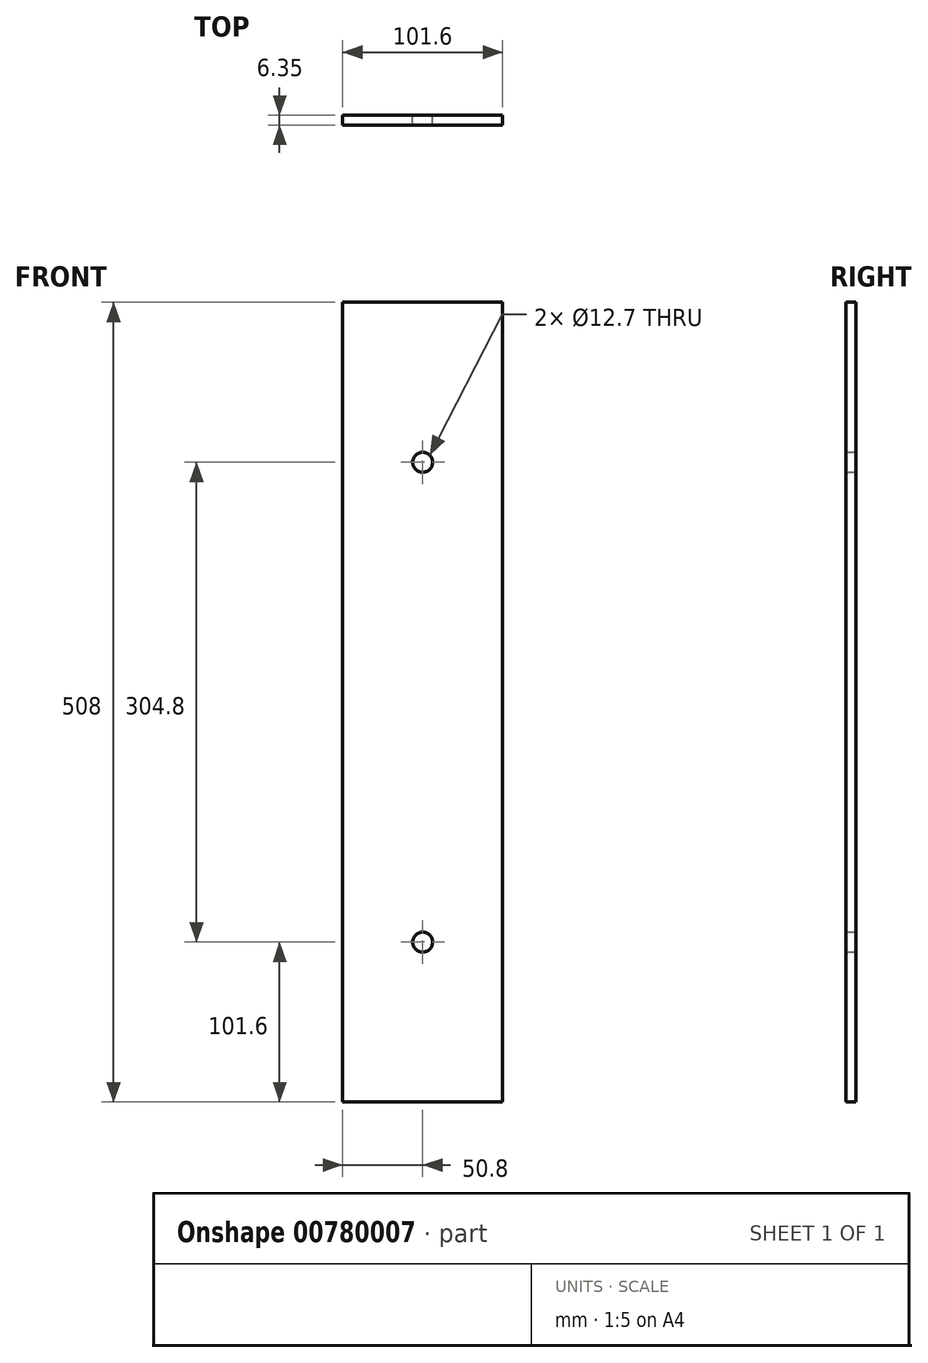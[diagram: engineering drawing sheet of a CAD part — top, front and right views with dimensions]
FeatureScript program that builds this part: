
annotation { "Feature Type Name" : "Feature", "Feature Type Description" : "" }
export const myFeature = defineFeature(function(context is Context, id is Id, definition is map)
    precondition{}
    {
        {
            var Q0;
            Q0=qCreatedBy(makeId("Front.planeOp"),FACE);
            var sketch = newSketch(context, id + "F0", { "sketchPlane" : qUnion([Q0])});
            skLineSegment(sketch, "E0.bottom", {"start": v(0, 0) * mm, "end": v(101.6, 0) * mm});
            skLineSegment(sketch, "E0.top", {"start": v(0, 508) * mm, "end": v(101.6, 508) * mm});
            skLineSegment(sketch, "E0.left", {"start": v(0, 0) * mm, "end": v(0, 508) * mm});
            skLineSegment(sketch, "E0.right", {"start": v(101.6, 0) * mm, "end": v(101.6, 508) * mm});
            skCircle(sketch, "E1", {"center": v(50.8, 101.6) * mm, "radius": 6.35 * mm});
            skPoint(sketch, "E1.centerSnap0", {"position": v(50.8, 0) * mm});
            skCircle(sketch, "E2", {"center": v(50.8, 406.4) * mm, "radius": 6.35 * mm});
            skPoint(sketch, "E2.centerSnap0", {"position": v(50.8, 508) * mm});
            skSolve(sketch);
        }
        {
            var Q0;
            Q0 = qSketchRegion(id + "F0", true);
            extrude(context, id + "F1", {"entities" : qUnion([Q0]), "depth" : 6.35 * mm, "offsetDistance" : 25.4 * mm});
        }
    });
